# Revit family: CAME_Турникет_Калитка_SALOON_505КомбинированнаяДляМГН
name_source: partatom
category: Специальное оборудование
units: mm (PartAtom-declared; Revit-internal decimal feet)

## family parameters
Всегда вертикально = Да
На основе рабочей плоскости = Нет
Общий = Нет
При загрузке вырезать с полостями = Нет
Размер круглого соединителя = Использовать диаметр
Тип детали = Нормальный
Точка расчета площади = Нет

## types (1)
- CAME_Турникет_Калитка_SALOON_505КомбинированнаяДляМГН
    ADSK_URL документации изделия = https://camerussia.com
    ADSK_URL страницы изделия = https://camerussia.com
    ADSK_Версия Revit = 2019
    ADSK_Версия семейства = 1.0
    ADSK_Группирование = SALOON
    ADSK_Единица измерения = шт.
    ADSK_Завод-изготовитель = CAME
    ADSK_Классификация нагрузок = Прочее
    ADSK_Код изделия = Код КСР 26.30.50.119.61.2.07.09
    ADSK_Количество = 1
    ADSK_Количество фаз = 1
    ADSK_Коэффициент мощности = 0.96
    ADSK_Марка = АРТ:001PSSL505ED
    ADSK_Масса = 56
    ADSK_Масса_Текст = 56 кг
    ADSK_Наименование = Турникет-калитка МГН моторизованная SALOON 505 двухпроходная комбинированная
    ADSK_Наименование краткое = Турникет-калитка МГН SALOON 505 комбинированная
    ADSK_Напряжение = 230 В
    ADSK_Номинальная мощность = 24 Вт
    ADSK_Обозначение = ТУ 26.30.50-001-89603926-2021
    ADSK_Полная мощность = 25 В·А
    ADSK_Размер_Высота = 955 мм
    ADSK_Размер_Глубина = 500 мм
    ADSK_Размер_Ширина = 1970 мм
    BL_BIM library = https://bimlib.pro
    CAME_Диапазон рабочих температур (°C) = -20 ÷ +68
    CAME_Интенсивность использования (%) = ИНТЕНСИВНОЕ
    CAME_Класс защиты (IP) = 54
    CAME_Максимальное количество проходов в минуту = 48
    CAME_Напряжение электропитания двигателя (В) = 24 В
    CAME_Тип механизма турникета = моторизованный
    URL = https://camerussia.com
    r = 17 мм
    Группа модели = Турникеты
    Изготовитель = CAME
    Минимальная ширина проема = 2020 мм
    Описание = Турникет-калитка для МГН моторизованная. Корпус и преграды - нержавеющая сталь AISI 304. Оснащена платой управления и светодиодными указателями прохода и направления. Сервопозиционный электропривод створки с определением препятствий и автоматической разблокировкой при отключении электроэнергии. Створка 900 мм с информационной вставкой. Комбинированная с турникетом-триподом моторизованным высокоинтенсивным STILE 500 с автоматической системой антипаники. Встроенный блок питания.
